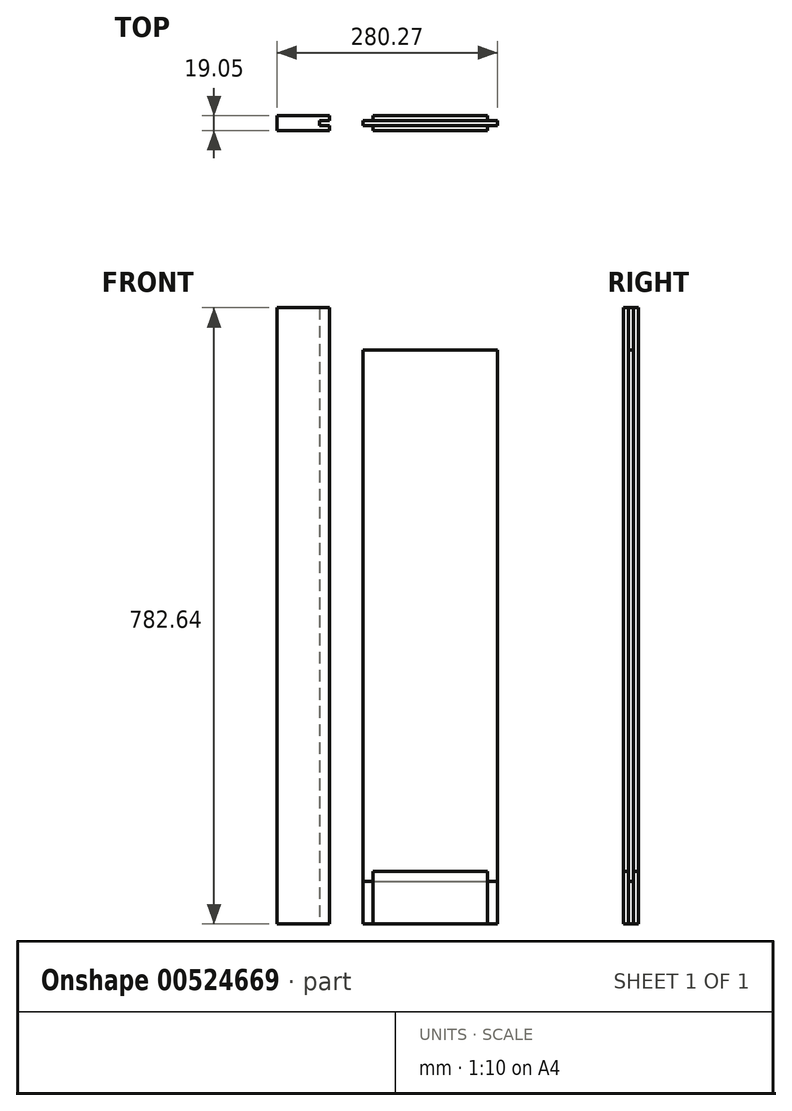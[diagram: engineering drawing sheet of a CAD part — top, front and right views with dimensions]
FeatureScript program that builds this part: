
annotation { "Feature Type Name" : "Feature", "Feature Type Description" : "" }
export const myFeature = defineFeature(function(context is Context, id is Id, definition is map)
    precondition{}
    {
        {
            var Q0;
            Q0=qCreatedBy(makeId("Front.planeOp"),FACE);
            var sketch = newSketch(context, id + "F0", { "sketchPlane" : qUnion([Q0])});
            skLineSegment(sketch, "E0.bottom", {"start": v(0, 782.64) * mm, "end": v(66.68, 782.64) * mm});
            skLineSegment(sketch, "E0.top", {"start": v(0, 0) * mm, "end": v(66.68, 0) * mm});
            skLineSegment(sketch, "E0.left", {"start": v(0, 782.64) * mm, "end": v(0, 0) * mm});
            skLineSegment(sketch, "E0.right", {"start": v(66.68, 782.64) * mm, "end": v(66.68, 0) * mm});
            skSolve(sketch);
        }
        {
            var Q0;
            Q0 = qSketchRegion(id + "F0", true);
            extrude(context, id + "F1", {"entities" : qUnion([Q0]), "depth" : 19.05 * mm, "offsetDistance" : 25.4 * mm});
        }
        {
            var Q0;
            Q0=makeQuery(id+"F1.opExtrude","SWEPT_FACE",FACE,{"disambiguationData":[OSD([sQuery(id+"F0.wireOp",EDGE,"E0.right")])]});
            var sketch = newSketch(context, id + "F2", { "sketchPlane" : qUnion([Q0])});
            skLineSegment(sketch, "E1", {"start": v(-9.53, 782.64) * mm, "end": v(-9.53, 616.94) * mm, "construction": true});
            skPoint(sketch, "E1.startSnap0", {"position": v(-9.53, 782.64) * mm});
            skLineSegment(sketch, "E2.bottom", {"start": v(-12.7, 782.64) * mm, "end": v(-6.35, 782.64) * mm});
            skLineSegment(sketch, "E2.top", {"start": v(-12.7, 0) * mm, "end": v(-6.35, 0) * mm});
            skLineSegment(sketch, "E2.left", {"start": v(-12.7, 782.64) * mm, "end": v(-12.7, 0) * mm});
            skLineSegment(sketch, "E2.right", {"start": v(-6.35, 782.64) * mm, "end": v(-6.35, 0) * mm});
            skSolve(sketch);
        }
        {
            var Q0;
            Q0 = qSketchRegion(id + "F2", true);
            extrude(context, id + "F3", {"entities" : qUnion([Q0]), "operationType" : NewBodyOperationType.REMOVE, "oppositeDirection" : true, "depth" : 12.7 * mm, "offsetDistance" : 25.4 * mm});
        }
        {
            var Q0;
            Q0=qCreatedBy(makeId("Front.planeOp"),FACE);
            var sketch = newSketch(context, id + "F4", { "sketchPlane" : qUnion([Q0])});
            skLineSegment(sketch, "E3.bottom", {"start": v(121.91, 66.67) * mm, "end": v(267.57, 66.67) * mm});
            skLineSegment(sketch, "E3.top", {"start": v(121.91, 0) * mm, "end": v(267.57, 0) * mm});
            skLineSegment(sketch, "E3.left", {"start": v(121.91, 66.67) * mm, "end": v(121.91, 0) * mm});
            skLineSegment(sketch, "E3.right", {"start": v(267.57, 66.67) * mm, "end": v(267.57, 0) * mm});
            skSolve(sketch);
        }
        {
            var Q0;
            Q0 = qSketchRegion(id + "F4", true);
            extrude(context, id + "F5", {"entities" : qUnion([Q0]), "depth" : 19.05 * mm, "offsetDistance" : 25.4 * mm});
        }
        {
            var Q0;
            Q0=makeQuery(id+"F5.opExtrude","SWEPT_FACE",FACE,{"disambiguationData":[OSD([sQuery(id+"F4.wireOp",EDGE,"E3.left")])]});
            var sketch = newSketch(context, id + "F6", { "sketchPlane" : qUnion([Q0])});
            skLineSegment(sketch, "E4", {"start": v(9.53, 66.67) * mm, "end": v(9.53, 22.37) * mm, "construction": true});
            skLineSegment(sketch, "E5.bottom", {"start": v(6.35, 66.67) * mm, "end": v(12.7, 66.67) * mm});
            skLineSegment(sketch, "E5.top", {"start": v(6.35, 0) * mm, "end": v(12.7, 0) * mm});
            skLineSegment(sketch, "E5.left", {"start": v(6.35, 66.67) * mm, "end": v(6.35, 0) * mm});
            skLineSegment(sketch, "E5.right", {"start": v(12.7, 66.67) * mm, "end": v(12.7, 0) * mm});
            skSolve(sketch);
        }
        {
            var Q0;
            Q0 = qSketchRegion(id + "F6", true);
            extrude(context, id + "F7", {"entities" : qUnion([Q0]), "operationType" : NewBodyOperationType.ADD, "depth" : 12.7 * mm, "offsetDistance" : 25.4 * mm});
        }
        {
            var Q0;
            Q0=makeQuery(id+"F5.opExtrude","SWEPT_FACE",FACE,{"disambiguationData":[OSD([sQuery(id+"F4.wireOp",EDGE,"E3.right")])]});
            var sketch = newSketch(context, id + "F8", { "sketchPlane" : qUnion([Q0])});
            skLineSegment(sketch, "E6.bottom", {"start": v(-12.7, 66.67) * mm, "end": v(-6.35, 66.67) * mm});
            skLineSegment(sketch, "E6.top", {"start": v(-12.7, 0) * mm, "end": v(-6.35, 0) * mm});
            skLineSegment(sketch, "E6.left", {"start": v(-12.7, 66.67) * mm, "end": v(-12.7, 0) * mm});
            skLineSegment(sketch, "E6.right", {"start": v(-6.35, 66.67) * mm, "end": v(-6.35, 0) * mm});
            skSolve(sketch);
        }
        {
            var Q0;
            Q0 = qSketchRegion(id + "F8", true);
            extrude(context, id + "F9", {"entities" : qUnion([Q0]), "operationType" : NewBodyOperationType.ADD, "depth" : 12.7 * mm, "offsetDistance" : 25.4 * mm});
        }
        {
            var Q0;
            Q0=makeQuery(id+"F9.boolean.opBoolean","MERGE",FACE,{"derivedFrom":[makeQuery(id+"F7.boolean.opBoolean","MERGE",FACE,{"derivedFrom":[makeQuery(id+"F5.opExtrude","SWEPT_FACE",FACE,{"disambiguationData":[OSD([sQuery(id+"F4.wireOp",EDGE,"E3.bottom")])]}),makeQuery(id+"F7.opExtrude","SWEPT_FACE",FACE,{"disambiguationData":[OSD([sQuery(id+"F6.wireOp",EDGE,"E5.bottom")])]})]}),makeQuery(id+"F9.opExtrude","SWEPT_FACE",FACE,{"disambiguationData":[OSD([sQuery(id+"F8.wireOp",EDGE,"E6.bottom")])]})]});
            var sketch = newSketch(context, id + "F10", { "sketchPlane" : qUnion([Q0])});
            skLineSegment(sketch, "E7.bottom", {"start": v(109.21, -6.35) * mm, "end": v(280.27, -6.35) * mm});
            skLineSegment(sketch, "E7.top", {"start": v(109.21, -12.7) * mm, "end": v(280.27, -12.7) * mm});
            skLineSegment(sketch, "E7.left", {"start": v(109.21, -6.35) * mm, "end": v(109.21, -12.7) * mm});
            skLineSegment(sketch, "E7.right", {"start": v(280.27, -6.35) * mm, "end": v(280.27, -12.7) * mm});
            skSolve(sketch);
        }
        {
            var Q0;
            Q0 = qSketchRegion(id + "F10", true);
            extrude(context, id + "F11", {"entities" : qUnion([Q0]), "operationType" : NewBodyOperationType.REMOVE, "oppositeDirection" : true, "depth" : 12.7 * mm, "offsetDistance" : 25.4 * mm});
        }
        {
            var Q0;
            Q0=makeQuery(id+"F9.opExtrude","SWEPT_FACE",FACE,{"disambiguationData":[OSD([sQuery(id+"F8.wireOp",EDGE,"E6.left")])]});
            var sketch = newSketch(context, id + "F12", { "sketchPlane" : qUnion([Q0])});
            skLineSegment(sketch, "E8.bottom", {"start": v(109.21, 728.66) * mm, "end": v(280.27, 728.66) * mm});
            skLineSegment(sketch, "E8.top", {"start": v(109.21, 53.97) * mm, "end": v(280.27, 53.97) * mm});
            skLineSegment(sketch, "E8.left", {"start": v(109.21, 728.66) * mm, "end": v(109.21, 53.97) * mm});
            skLineSegment(sketch, "E8.right", {"start": v(280.27, 728.66) * mm, "end": v(280.27, 53.97) * mm});
            skSolve(sketch);
        }
        {
            var Q0;
            Q0 = qSketchRegion(id + "F12", true);
            var Q1;
            Q1=makeQuery(id+"F9.opExtrude","SWEPT_FACE",FACE,{"disambiguationData":[OSD([sQuery(id+"F8.wireOp",EDGE,"E6.right")])]});
            extrude(context, id + "F13", {"entities" : qUnion([Q0]), "endBound" : BoundingType.UP_TO_SURFACE, "oppositeDirection" : true, "depth" : 25.4 * mm, "endBoundEntityFace" : qUnion([Q1]), "offsetDistance" : 25.4 * mm});
        }
    });
